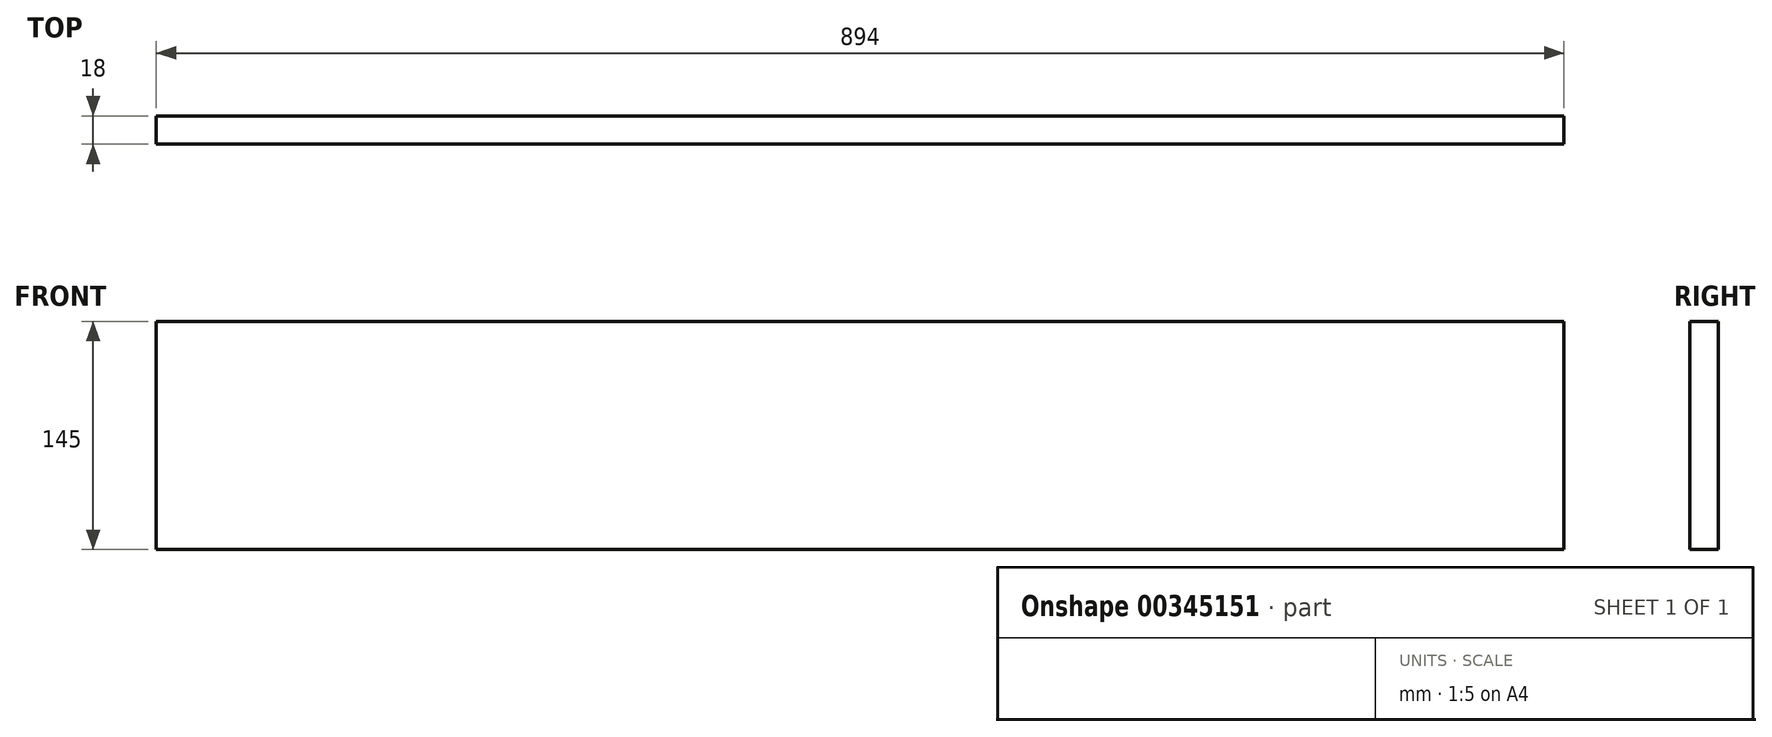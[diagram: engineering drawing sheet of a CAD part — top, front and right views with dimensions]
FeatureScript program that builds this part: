
annotation { "Feature Type Name" : "Feature", "Feature Type Description" : "" }
export const myFeature = defineFeature(function(context is Context, id is Id, definition is map)
    precondition{}
    {
        {
            var Q0;
            Q0=qCreatedBy(makeId("Front.planeOp"),FACE);
            var sketch = newSketch(context, id + "F0", { "sketchPlane" : qUnion([Q0])});
            skLineSegment(sketch, "E0.bottom", {"start": v(0, 0) * mm, "end": v(51.96, 0) * mm});
            skLineSegment(sketch, "E0.top", {"start": v(0, 41.5) * mm, "end": v(51.96, 41.5) * mm});
            skLineSegment(sketch, "E0.left", {"start": v(0, 0) * mm, "end": v(0, 41.5) * mm});
            skLineSegment(sketch, "E0.right", {"start": v(51.96, 0) * mm, "end": v(51.96, 41.5) * mm});
            skSolve(sketch);
        }
        {
            var Q0;
            Q0=makeQuery(id+"F0.imprint","IMPRINT",FACE,{"disambiguationData":[TD([[makeQuery(id+"F0.imprint","IMPRINT",EDGE,{"derivedFrom":sQuery(id+"F0.wireOp",EDGE,"E0.bottom")}),1.0]])]});
            extrude(context, id + "F1", {"entities" : qUnion([Q0]), "depth" : 18 * mm});
        }
        {
            var Q0;
            Q0=makeQuery(id+"F1.opExtrude","SWEPT_FACE",FACE,{"disambiguationData":[OSD([sQuery(id+"F0.wireOp",EDGE,"E0.bottom")])]});
            extrude(context, id + "F2", {"entities" : qUnion([Q0]), "operationType" : NewBodyOperationType.ADD, "oppositeDirection" : true, "depth" : 145 * mm});
        }
        {
            var Q0;
            {var subQ0=sQuery(id+"F0.wireOp",EDGE,"E0.left");Q0=makeQuery(id+"F2.boolean.opBoolean","MERGE",FACE,{"derivedFrom":[makeQuery(id+"F1.opExtrude","SWEPT_FACE",FACE,{"disambiguationData":[OSD([subQ0])]}),makeQuery(id+"F2.opExtrude","SWEPT_FACE",FACE,{"disambiguationData":[OSD([sQuery(id+"F0.wireOp",EDGE,"E0.bottom"),subQ0])]})]});}
            extrude(context, id + "F3", {"entities" : qUnion([Q0]), "operationType" : NewBodyOperationType.ADD, "oppositeDirection" : true, "depth" : 896 * mm});
        }
        {
            var Q0;
            {var subQ0=sQuery(id+"F0.wireOp",EDGE,"E0.left");Q0=makeQuery(id+"F2.boolean.opBoolean","MERGE",FACE,{"derivedFrom":[makeQuery(id+"F1.opExtrude","SWEPT_FACE",FACE,{"disambiguationData":[OSD([subQ0])]}),makeQuery(id+"F2.opExtrude","SWEPT_FACE",FACE,{"disambiguationData":[OSD([sQuery(id+"F0.wireOp",EDGE,"E0.bottom"),subQ0])]})]});}
            extrude(context, id + "F4", {"entities" : qUnion([Q0]), "operationType" : NewBodyOperationType.ADD, "oppositeDirection" : true, "depth" : 896 * mm});
        }
        {
            var Q0;
            Q0=makeQuery(id+"F3.opExtrude","CAP_FACE",FACE,{"disambiguationData":[OSD([sQuery(id+"F0.wireOp",EDGE,"E0.bottom"),sQuery(id+"F0.wireOp",EDGE,"E0.left")])],"isStart":false});
            extrude(context, id + "F5", {"entities" : qUnion([Q0]), "operationType" : NewBodyOperationType.REMOVE, "oppositeDirection" : true, "depth" : 2 * mm});
        }
    });
